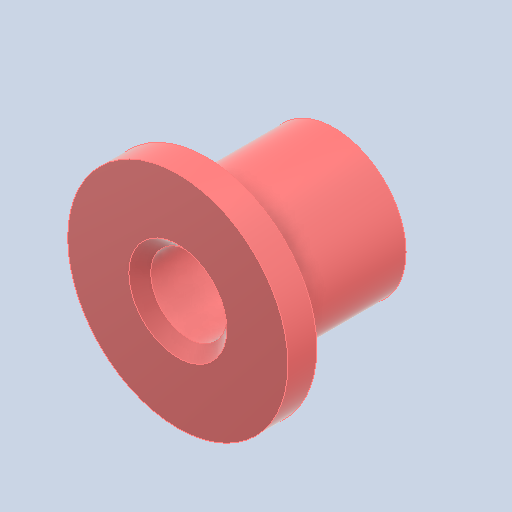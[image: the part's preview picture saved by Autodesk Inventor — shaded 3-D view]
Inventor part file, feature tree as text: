
AUTODESK INVENTOR PART (.ipt)
format: ipt  version: 2022 (Build 260153000, 153)  size: 122,880 bytes
history: native  units: in
note: dims shown in document units (in); Inventor stores cm internally (conversion verified against a paired STEP export)
features: other x3, sketch x2
ambient origin geometry x8: Origin, YZ Plane, XZ Plane, XY Plane, X Axis, Y Axis, Z Axis, Center Point
bodies: Solid1 (feature_tree)
feature tree (5):
  other  "bearingsleeve.ipt"
  other  "Solid1::bearingsleeve.ipt"
  other  "TaggingFeature1"
  sketch  "Sketch1"  dims[d0=0.3937in]
  sketch  "Sketch2"
